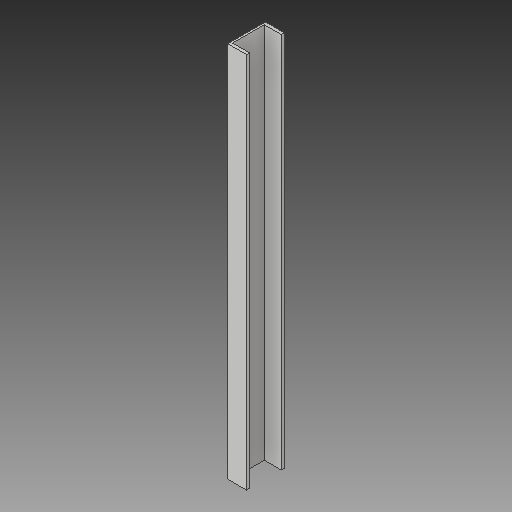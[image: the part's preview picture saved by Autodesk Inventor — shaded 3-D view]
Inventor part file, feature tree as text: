
AUTODESK INVENTOR PART (.ipt)
format: ipt  version: 2019 (Build 230136000, 136)  size: 90,112 bytes
history: native  units: in
note: dims shown in document units (in); Inventor stores cm internally (conversion verified against a paired STEP export)
features: other x3, sketch x1
ambient origin geometry x8: Origin, YZ Plane, XZ Plane, XY Plane, X Axis, Y Axis, Z Axis, Center Point
bodies: Solid1 (feature_tree)
feature tree (4):
  other  "Channel1.ipt"
  other  "Solid1::Channel1.ipt"
  other  "TaggingFeature1"
  sketch  "Sketch1"  dims[d0=0.3937in]
